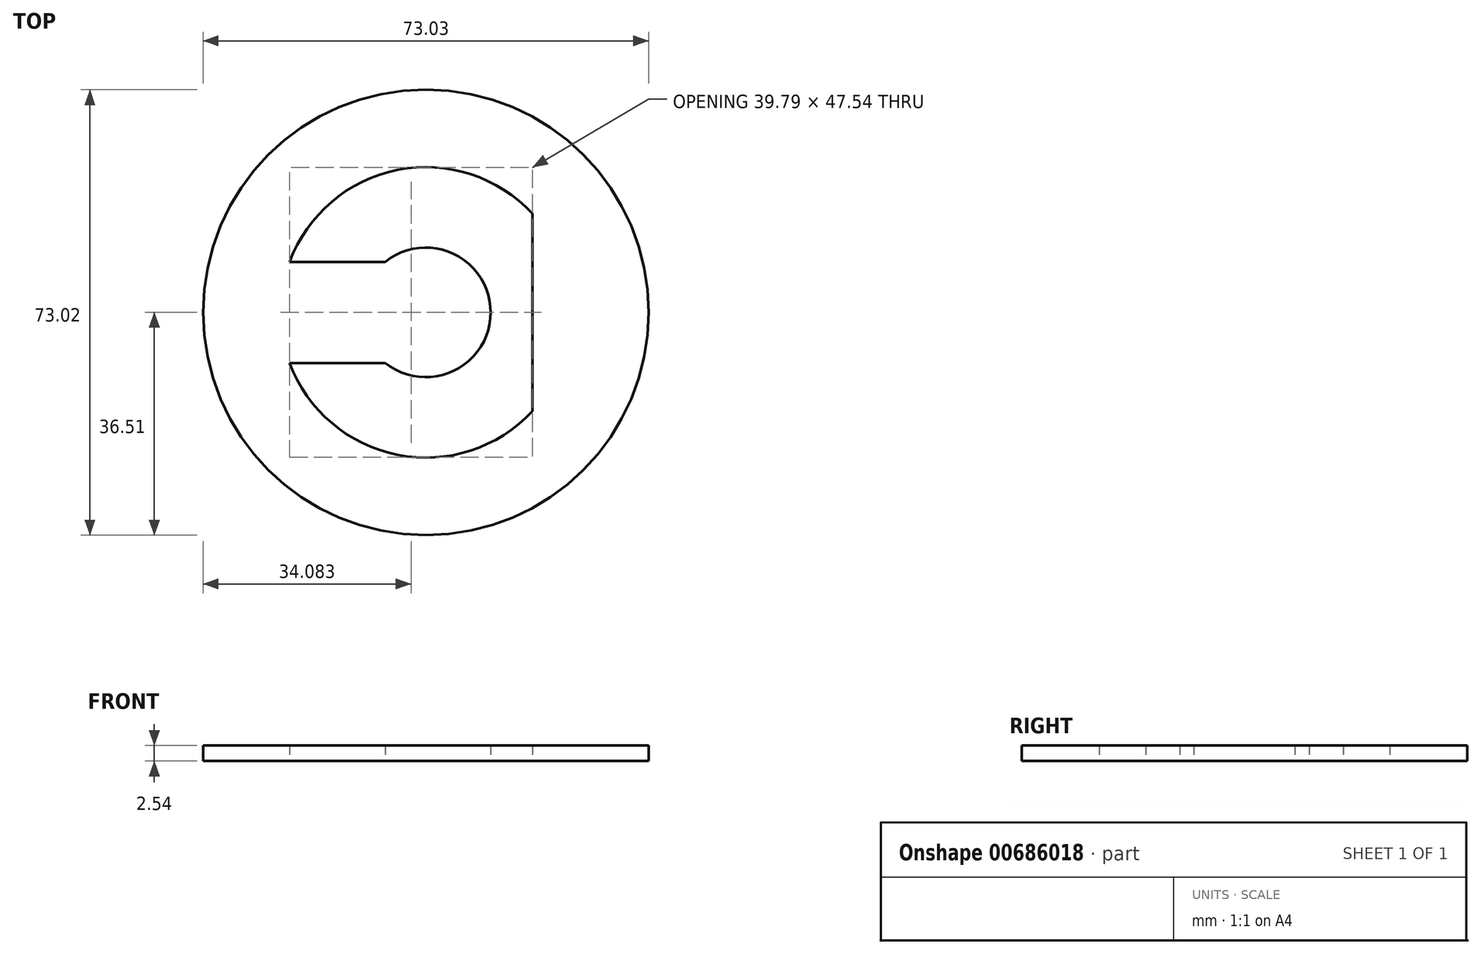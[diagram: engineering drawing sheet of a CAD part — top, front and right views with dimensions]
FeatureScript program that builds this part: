
annotation { "Feature Type Name" : "Feature", "Feature Type Description" : "" }
export const myFeature = defineFeature(function(context is Context, id is Id, definition is map)
    precondition{}
    {
        {
            var Q0;
            Q0=qCreatedBy(makeId("Top.planeOp"),FACE);
            var sketch = newSketch(context, id + "F0", { "sketchPlane" : qUnion([Q0])});
            skLineSegment(sketch, "E0.0", {"start": v(19.69, -16.19) * mm, "end": v(19.69, 16.19) * mm});
            skLineSegment(sketch, "E0.1", {"start": v(-4.41, 8.29) * mm, "end": v(-20.1, 8.29) * mm});
            skArc(sketch, "E0.2", {"start": v(-4.41, -8.29) * mm, "mid": v(12.84, 0) * mm, "end": v(-4.41, 8.29) * mm});
            skArc(sketch, "E0.3", {"start": v(19.69, 16.19) * mm, "mid": v(-2.42, 23.36) * mm, "end": v(-20.1, 8.29) * mm});
            skLineSegment(sketch, "E0.4", {"start": v(-4.41, -8.29) * mm, "end": v(-20.1, -8.29) * mm});
            skArc(sketch, "E0.5", {"start": v(-20.1, -8.29) * mm, "mid": v(-2.42, -23.36) * mm, "end": v(19.69, -16.19) * mm});
            skCircle(sketch, "E1.0", {"center": v(2.22, 0) * mm, "radius": 36.51 * mm});
            skSolve(sketch);
        }
        {
            var Q0;
            Q0=makeQuery(id+"F0.imprint","IMPRINT",FACE,{"disambiguationData":[TD([[makeQuery(id+"F0.imprint","IMPRINT",EDGE,{"derivedFrom":sQuery(id+"F0.wireOp",EDGE,"E0.0")}),-1.0]])]});
            extrude(context, id + "F1", {"entities" : qUnion([Q0]), "depth" : 2.54 * mm, "offsetDistance" : 25.4 * mm});
        }
    });
